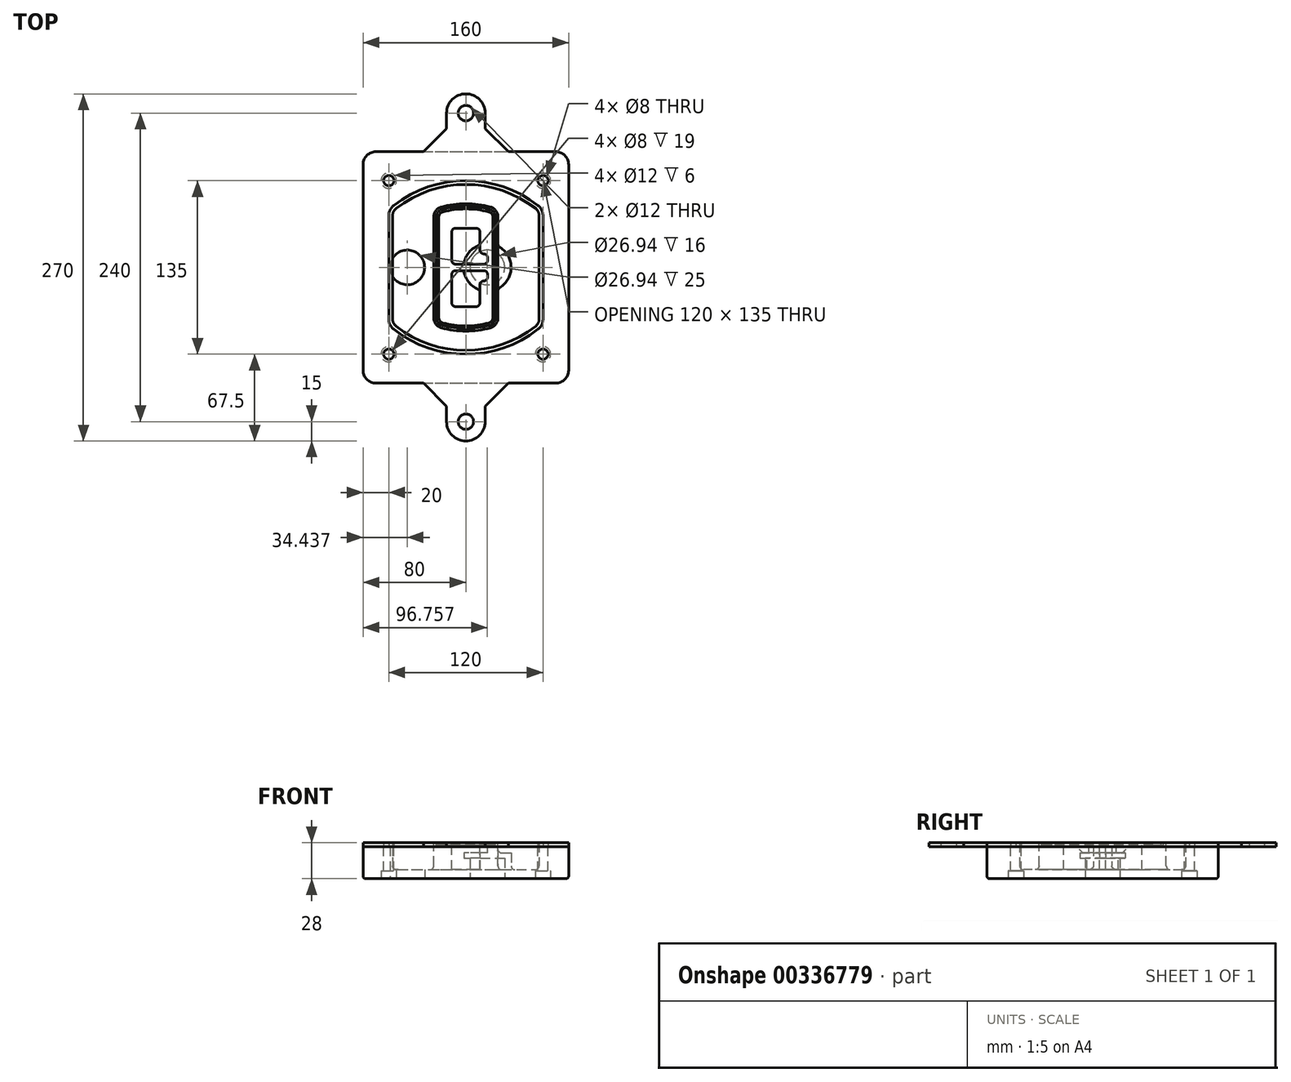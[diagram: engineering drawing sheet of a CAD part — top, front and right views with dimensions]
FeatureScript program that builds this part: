
annotation { "Feature Type Name" : "Feature", "Feature Type Description" : "" }
export const myFeature = defineFeature(function(context is Context, id is Id, definition is map)
    precondition{}
    {
        {
            var Q0;
            Q0=qCreatedBy(makeId("Top.planeOp"),FACE);
            var sketch = newSketch(context, id + "F0", { "sketchPlane" : qUnion([Q0])});
            skPoint(sketch, "E0.rect.middle", {"position": v(0, 0) * mm});
            skLineSegment(sketch, "E1.bottom", {"start": v(-70, -90) * mm, "end": v(70, -90) * mm});
            skLineSegment(sketch, "E1.top", {"start": v(-70, 90) * mm, "end": v(70, 90) * mm});
            skLineSegment(sketch, "E1.left", {"start": v(-80, -80) * mm, "end": v(-80, 80) * mm});
            skLineSegment(sketch, "E1.right", {"start": v(80, -80) * mm, "end": v(80, 80) * mm});
            skLineSegment(sketch, "E2", {"start": v(-80, 90) * mm, "end": v(80, -90) * mm, "construction": true});
            skLineSegment(sketch, "E3", {"start": v(80, 90) * mm, "end": v(-80, -90) * mm, "construction": true});
            skCircle(sketch, "E4", {"center": v(-60, 67.5) * mm, "radius": 4 * mm});
            skCircle(sketch, "E5", {"center": v(60, 67.5) * mm, "radius": 4 * mm});
            skCircle(sketch, "E6", {"center": v(60, -67.5) * mm, "radius": 4 * mm});
            skCircle(sketch, "E7", {"center": v(-60, -67.5) * mm, "radius": 4 * mm});
            skLineSegment(sketch, "E8", {"start": v(-60, 67.5) * mm, "end": v(60, 67.5) * mm, "construction": true});
            skLineSegment(sketch, "E9", {"start": v(60, 67.5) * mm, "end": v(60, -67.5) * mm, "construction": true});
            skLineSegment(sketch, "E10", {"start": v(60, -67.5) * mm, "end": v(-60, -67.5) * mm, "construction": true});
            skLineSegment(sketch, "E11", {"start": v(-60, -67.5) * mm, "end": v(-60, 67.5) * mm, "construction": true});
            skLineSegment(sketch, "E12", {"start": v(-60, 40.3) * mm, "end": v(-60, -40.3) * mm});
            skLineSegment(sketch, "E13", {"start": v(60, 40.3) * mm, "end": v(60, -40.3) * mm});
            skArc(sketch, "E14", {"start": v(56.15, 48.18) * mm, "mid": v(0, 67.5) * mm, "end": v(-56.15, 48.18) * mm});
            skArc(sketch, "E15", {"start": v(-56.15, -48.18) * mm, "mid": v(0, -67.5) * mm, "end": v(56.15, -48.18) * mm});
            skLineSegment(sketch, "E16", {"start": v(-60, 0) * mm, "end": v(60, 0) * mm, "construction": true});
            skPoint(sketch, "E17.visualSharp", {"position": v(-60, -45) * mm});
            skArc(sketch, "E17.filletArc", {"start": v(-60, -40.3) * mm, "mid": v(-58.99, -44.68) * mm, "end": v(-56.15, -48.18) * mm});
            skPoint(sketch, "E18.visualSharp", {"position": v(-60, 45) * mm});
            skArc(sketch, "E18.filletArc", {"start": v(-56.15, 48.18) * mm, "mid": v(-58.99, 44.68) * mm, "end": v(-60, 40.3) * mm});
            skPoint(sketch, "E19.visualSharp", {"position": v(60, 45) * mm});
            skArc(sketch, "E19.filletArc", {"start": v(60, 40.3) * mm, "mid": v(58.99, 44.68) * mm, "end": v(56.15, 48.18) * mm});
            skPoint(sketch, "E20.visualSharp", {"position": v(60, -45) * mm});
            skArc(sketch, "E20.filletArc", {"start": v(56.15, -48.18) * mm, "mid": v(58.99, -44.68) * mm, "end": v(60, -40.3) * mm});
            skPoint(sketch, "E21.visualSharp", {"position": v(-80, 90) * mm});
            skArc(sketch, "E21.filletArc", {"start": v(-70, 90) * mm, "mid": v(-77.07, 87.07) * mm, "end": v(-80, 80) * mm});
            skPoint(sketch, "E22.visualSharp", {"position": v(80, 90) * mm});
            skArc(sketch, "E22.filletArc", {"start": v(80, 80) * mm, "mid": v(77.07, 87.07) * mm, "end": v(70, 90) * mm});
            skPoint(sketch, "E23.visualSharp", {"position": v(80, -90) * mm});
            skArc(sketch, "E23.filletArc", {"start": v(70, -90) * mm, "mid": v(77.07, -87.07) * mm, "end": v(80, -80) * mm});
            skPoint(sketch, "E24.visualSharp", {"position": v(-80, -90) * mm});
            skArc(sketch, "E24.filletArc", {"start": v(-80, -80) * mm, "mid": v(-77.07, -87.07) * mm, "end": v(-70, -90) * mm});
            skArc(sketch, "E25.0", {"start": v(57, 40.3) * mm, "mid": v(56.3, 43.36) * mm, "end": v(54.3, 45.81) * mm});
            skLineSegment(sketch, "E25.1", {"start": v(57, 40.3) * mm, "end": v(57, -40.3) * mm});
            skArc(sketch, "E25.2", {"start": v(54.3, -45.81) * mm, "mid": v(56.3, -43.36) * mm, "end": v(57, -40.3) * mm});
            skArc(sketch, "E25.3", {"start": v(-54.3, -45.81) * mm, "mid": v(0, -64.5) * mm, "end": v(54.3, -45.81) * mm});
            skArc(sketch, "E25.4", {"start": v(-57, -40.3) * mm, "mid": v(-56.3, -43.36) * mm, "end": v(-54.3, -45.81) * mm});
            skArc(sketch, "E25.5", {"start": v(54.3, 45.81) * mm, "mid": v(0, 64.5) * mm, "end": v(-54.3, 45.81) * mm});
            skLineSegment(sketch, "E25.6", {"start": v(-57, 40.3) * mm, "end": v(-57, -40.3) * mm});
            skArc(sketch, "E25.7", {"start": v(-54.3, 45.81) * mm, "mid": v(-56.3, 43.36) * mm, "end": v(-57, 40.3) * mm});
            skArc(sketch, "E26.0", {"start": v(-58.62, 51.33) * mm, "mid": v(-62.58, 46.43) * mm, "end": v(-64, 40.3) * mm});
            skArc(sketch, "E26.1", {"start": v(58.62, 51.33) * mm, "mid": v(0, 71.5) * mm, "end": v(-58.62, 51.33) * mm});
            skArc(sketch, "E26.2", {"start": v(64, 40.3) * mm, "mid": v(62.58, 46.43) * mm, "end": v(58.62, 51.33) * mm});
            skLineSegment(sketch, "E26.3", {"start": v(64, 40.3) * mm, "end": v(64, -40.3) * mm});
            skArc(sketch, "E26.4", {"start": v(58.62, -51.33) * mm, "mid": v(62.58, -46.43) * mm, "end": v(64, -40.3) * mm});
            skLineSegment(sketch, "E26.5", {"start": v(-64, 40.3) * mm, "end": v(-64, -40.3) * mm});
            skArc(sketch, "E26.6", {"start": v(-58.62, -51.33) * mm, "mid": v(0, -71.5) * mm, "end": v(58.62, -51.33) * mm});
            skArc(sketch, "E26.7", {"start": v(-64, -40.3) * mm, "mid": v(-62.58, -46.43) * mm, "end": v(-58.62, -51.33) * mm});
            skSolve(sketch);
        }
        {
            var Q0;
            Q0=makeQuery(id+"F0.imprint","IMPRINT",FACE,{"disambiguationData":[TD([[makeQuery(id+"F0.imprint","IMPRINT",EDGE,{"derivedFrom":sQuery(id+"F0.wireOp",EDGE,"E1.bottom")}),1.0]])]});
            var Q1;
            Q1=makeQuery(id+"F0.imprint","IMPRINT",FACE,{"disambiguationData":[TD([[makeQuery(id+"F0.imprint","IMPRINT",EDGE,{"derivedFrom":sQuery(id+"F0.wireOp",EDGE,"E12")}),1.0]])]});
            var Q2;
            Q2=makeQuery(id+"F0.imprint","IMPRINT",FACE,{"disambiguationData":[TD([[makeQuery(id+"F0.imprint","IMPRINT",EDGE,{"derivedFrom":sQuery(id+"F0.wireOp",EDGE,"E25.0")}),1.0]])]});
            var Q3;
            Q3=makeQuery(id+"F0.imprint","IMPRINT",FACE,{"disambiguationData":[TD([[makeQuery(id+"F0.imprint","IMPRINT",EDGE,{"derivedFrom":sQuery(id+"F0.wireOp",EDGE,"E12")}),-1.0]])]});
            extrude(context, id + "F1", {"entities" : qUnion([Q0, Q1, Q2, Q3]), "oppositeDirection" : true, "depth" : 25 * mm});
        }
        {
            var Q0;
            Q0=makeQuery(id+"F0.imprint","IMPRINT",FACE,{"disambiguationData":[TD([[makeQuery(id+"F0.imprint","IMPRINT",EDGE,{"derivedFrom":sQuery(id+"F0.wireOp",EDGE,"E12")}),1.0]])]});
            extrude(context, id + "F2", {"entities" : qUnion([Q0]), "operationType" : NewBodyOperationType.ADD, "depth" : 3 * mm});
        }
        {
            var Q0;
            Q0=makeQuery(id+"F0.imprint","IMPRINT",FACE,{"disambiguationData":[TD([[makeQuery(id+"F0.imprint","IMPRINT",EDGE,{"derivedFrom":sQuery(id+"F0.wireOp",EDGE,"E25.0")}),1.0]])]});
            extrude(context, id + "F3", {"entities" : qUnion([Q0]), "operationType" : NewBodyOperationType.REMOVE, "oppositeDirection" : true, "depth" : 18 * mm});
        }
        {
            var Q0;
            Q0=makeQuery(id+"F2.opExtrude","CAP_FACE",FACE,{"disambiguationData":[OSD([sQuery(id+"F0.wireOp",EDGE,"E12"),sQuery(id+"F0.wireOp",EDGE,"E13"),sQuery(id+"F0.wireOp",EDGE,"E14"),sQuery(id+"F0.wireOp",EDGE,"E15"),sQuery(id+"F0.wireOp",EDGE,"E17.filletArc"),sQuery(id+"F0.wireOp",EDGE,"E18.filletArc"),sQuery(id+"F0.wireOp",EDGE,"E19.filletArc"),sQuery(id+"F0.wireOp",EDGE,"E20.filletArc"),sQuery(id+"F0.wireOp",EDGE,"E25.0"),sQuery(id+"F0.wireOp",EDGE,"E25.1"),sQuery(id+"F0.wireOp",EDGE,"E25.2"),sQuery(id+"F0.wireOp",EDGE,"E25.3"),sQuery(id+"F0.wireOp",EDGE,"E25.4"),sQuery(id+"F0.wireOp",EDGE,"E25.5"),sQuery(id+"F0.wireOp",EDGE,"E25.6"),sQuery(id+"F0.wireOp",EDGE,"E25.7")])],"isStart":false});
            var sketch = newSketch(context, id + "F4", { "sketchPlane" : qUnion([Q0])});
            skArc(sketch, "E27.0", {"start": v(-19.08, -46.97) * mm, "mid": v(0, -49.5) * mm, "end": v(19.08, -46.97) * mm});
            skArc(sketch, "E28.0", {"start": v(19.08, 46.97) * mm, "mid": v(0, 49.5) * mm, "end": v(-19.08, 46.97) * mm});
            skLineSegment(sketch, "E29", {"start": v(-25, 39.25) * mm, "end": v(-25, -39.25) * mm});
            skLineSegment(sketch, "E30", {"start": v(25, 39.25) * mm, "end": v(25, -39.25) * mm});
            skLineSegment(sketch, "E31", {"start": v(-25, 45.1) * mm, "end": v(25, 45.1) * mm, "construction": true});
            skLineSegment(sketch, "E32", {"start": v(-25, -45.1) * mm, "end": v(25, -45.1) * mm, "construction": true});
            skPoint(sketch, "E33.visualSharp", {"position": v(-25, 45.1) * mm});
            skArc(sketch, "E33.filletArc", {"start": v(-19.08, 46.97) * mm, "mid": v(-23.35, 44.11) * mm, "end": v(-25, 39.25) * mm});
            skPoint(sketch, "E34.visualSharp", {"position": v(25, 45.1) * mm});
            skArc(sketch, "E34.filletArc", {"start": v(25, 39.25) * mm, "mid": v(23.35, 44.11) * mm, "end": v(19.08, 46.97) * mm});
            skPoint(sketch, "E35.visualSharp", {"position": v(25, -45.1) * mm});
            skArc(sketch, "E35.filletArc", {"start": v(19.08, -46.97) * mm, "mid": v(23.35, -44.11) * mm, "end": v(25, -39.25) * mm});
            skPoint(sketch, "E36.visualSharp", {"position": v(-25, -45.1) * mm});
            skArc(sketch, "E36.filletArc", {"start": v(-25, -39.25) * mm, "mid": v(-23.35, -44.11) * mm, "end": v(-19.08, -46.97) * mm});
            skArc(sketch, "E37.0", {"start": v(54.3, 45.81) * mm, "mid": v(0, 64.5) * mm, "end": v(-54.3, 45.81) * mm});
            skArc(sketch, "E37.1", {"start": v(-54.3, 45.81) * mm, "mid": v(-56.3, 43.36) * mm, "end": v(-57, 40.3) * mm});
            skLineSegment(sketch, "E37.2", {"start": v(-57, 40.3) * mm, "end": v(-57, -40.3) * mm});
            skArc(sketch, "E37.3", {"start": v(-57, -40.3) * mm, "mid": v(-56.3, -43.36) * mm, "end": v(-54.3, -45.81) * mm});
            skArc(sketch, "E37.4", {"start": v(-54.3, -45.81) * mm, "mid": v(0, -64.5) * mm, "end": v(54.3, -45.81) * mm});
            skArc(sketch, "E37.5", {"start": v(54.3, -45.81) * mm, "mid": v(56.3, -43.36) * mm, "end": v(57, -40.3) * mm});
            skLineSegment(sketch, "E37.6", {"start": v(57, 40.3) * mm, "end": v(57, -40.3) * mm});
            skArc(sketch, "E37.7", {"start": v(57, 40.3) * mm, "mid": v(56.3, 43.36) * mm, "end": v(54.3, 45.81) * mm});
            skLineSegment(sketch, "E38.0", {"start": v(23, 39.25) * mm, "end": v(23, -39.25) * mm});
            skArc(sketch, "E38.1", {"start": v(18.56, -45.04) * mm, "mid": v(21.76, -42.9) * mm, "end": v(23, -39.25) * mm});
            skArc(sketch, "E38.2", {"start": v(-18.56, -45.04) * mm, "mid": v(0, -47.5) * mm, "end": v(18.56, -45.04) * mm});
            skArc(sketch, "E38.3", {"start": v(-23, -39.25) * mm, "mid": v(-21.76, -42.9) * mm, "end": v(-18.56, -45.04) * mm});
            skLineSegment(sketch, "E38.4", {"start": v(-23, 39.25) * mm, "end": v(-23, -39.25) * mm});
            skArc(sketch, "E38.5", {"start": v(23, 39.25) * mm, "mid": v(21.76, 42.9) * mm, "end": v(18.56, 45.04) * mm});
            skArc(sketch, "E38.6", {"start": v(-18.56, 45.04) * mm, "mid": v(-21.76, 42.9) * mm, "end": v(-23, 39.25) * mm});
            skArc(sketch, "E38.7", {"start": v(18.56, 45.04) * mm, "mid": v(0, 47.5) * mm, "end": v(-18.56, 45.04) * mm});
            skArc(sketch, "E39.0", {"start": v(21, 39.25) * mm, "mid": v(20.18, 41.68) * mm, "end": v(18.04, 43.1) * mm});
            skLineSegment(sketch, "E39.1", {"start": v(21, 39.25) * mm, "end": v(21, -39.25) * mm});
            skArc(sketch, "E39.2", {"start": v(18.04, -43.1) * mm, "mid": v(20.18, -41.68) * mm, "end": v(21, -39.25) * mm});
            skArc(sketch, "E39.3", {"start": v(-18.04, -43.1) * mm, "mid": v(0, -45.5) * mm, "end": v(18.04, -43.1) * mm});
            skArc(sketch, "E39.4", {"start": v(-21, -39.25) * mm, "mid": v(-20.18, -41.68) * mm, "end": v(-18.04, -43.1) * mm});
            skArc(sketch, "E39.5", {"start": v(18.04, 43.1) * mm, "mid": v(0, 45.5) * mm, "end": v(-18.04, 43.1) * mm});
            skLineSegment(sketch, "E39.6", {"start": v(-21, 39.25) * mm, "end": v(-21, -39.25) * mm});
            skArc(sketch, "E39.7", {"start": v(-18.04, 43.1) * mm, "mid": v(-20.18, 41.68) * mm, "end": v(-21, 39.25) * mm});
            skLineSegment(sketch, "E40", {"start": v(-25, 0) * mm, "end": v(25, 0) * mm, "construction": true});
            skLineSegment(sketch, "E41", {"start": v(-11, 5.5) * mm, "end": v(-11, 27.5) * mm});
            skLineSegment(sketch, "E42", {"start": v(-8, 30.5) * mm, "end": v(8, 30.5) * mm});
            skLineSegment(sketch, "E43", {"start": v(11, 27.5) * mm, "end": v(11, 13.5) * mm});
            skLineSegment(sketch, "E44", {"start": v(14, 10.5) * mm, "end": v(14, 10.5) * mm});
            skLineSegment(sketch, "E45", {"start": v(17, 7.5) * mm, "end": v(17, 5.5) * mm});
            skLineSegment(sketch, "E46", {"start": v(14, 2.5) * mm, "end": v(-8, 2.5) * mm});
            skPoint(sketch, "E47.visualSharp", {"position": v(-11, 30.5) * mm});
            skArc(sketch, "E47.filletArc", {"start": v(-8, 30.5) * mm, "mid": v(-10.12, 29.62) * mm, "end": v(-11, 27.5) * mm});
            skPoint(sketch, "E48.visualSharp", {"position": v(11, 30.5) * mm});
            skArc(sketch, "E48.filletArc", {"start": v(11, 27.5) * mm, "mid": v(10.12, 29.62) * mm, "end": v(8, 30.5) * mm});
            skPoint(sketch, "E49.visualSharp", {"position": v(11, 10.5) * mm});
            skArc(sketch, "E49.filletArc", {"start": v(11, 13.5) * mm, "mid": v(11.88, 11.38) * mm, "end": v(14, 10.5) * mm});
            skPoint(sketch, "E50.visualSharp", {"position": v(17, 10.5) * mm});
            skArc(sketch, "E50.filletArc", {"start": v(17, 7.5) * mm, "mid": v(16.12, 9.62) * mm, "end": v(14, 10.5) * mm});
            skPoint(sketch, "E51.visualSharp", {"position": v(17, 2.5) * mm});
            skArc(sketch, "E51.filletArc", {"start": v(14, 2.5) * mm, "mid": v(16.12, 3.38) * mm, "end": v(17, 5.5) * mm});
            skPoint(sketch, "E52.visualSharp", {"position": v(-11, 2.5) * mm});
            skArc(sketch, "E52.filletArc", {"start": v(-11, 5.5) * mm, "mid": v(-10.12, 3.38) * mm, "end": v(-8, 2.5) * mm});
            skLineSegment(sketch, "E53.0.MirrorCS", {"start": v(14, -2.5) * mm, "end": v(-8, -2.5) * mm});
            skArc(sketch, "E54.0.MirrorCS", {"start": v(-11, -5.5) * mm, "mid": v(-10.12, -3.38) * mm, "end": v(-8, -2.5) * mm});
            skLineSegment(sketch, "E55.0.MirrorCS", {"start": v(-11, -5.5) * mm, "end": v(-11, -27.5) * mm});
            skArc(sketch, "E56.0.MirrorCS", {"start": v(-8, -30.5) * mm, "mid": v(-10.12, -29.62) * mm, "end": v(-11, -27.5) * mm});
            skLineSegment(sketch, "E57.0.MirrorCS", {"start": v(-8, -30.5) * mm, "end": v(8, -30.5) * mm});
            skArc(sketch, "E58.0.MirrorCS", {"start": v(11, -27.5) * mm, "mid": v(10.12, -29.62) * mm, "end": v(8, -30.5) * mm});
            skLineSegment(sketch, "E59.0.MirrorCS", {"start": v(11, -27.5) * mm, "end": v(11, -13.5) * mm});
            skArc(sketch, "E60.0.MirrorCS", {"start": v(11, -13.5) * mm, "mid": v(11.88, -11.38) * mm, "end": v(14, -10.5) * mm});
            skArc(sketch, "E61.0.MirrorCS", {"start": v(17, -7.5) * mm, "mid": v(16.12, -9.62) * mm, "end": v(14, -10.5) * mm});
            skLineSegment(sketch, "E62.0.MirrorCS", {"start": v(17, -7.5) * mm, "end": v(17, -5.5) * mm});
            skArc(sketch, "E63.0.MirrorCS", {"start": v(14, -2.5) * mm, "mid": v(16.12, -3.38) * mm, "end": v(17, -5.5) * mm});
            skSolve(sketch);
        }
        {
            var Q0;
            Q0=makeQuery(id+"F4.imprint","IMPRINT",FACE,{"disambiguationData":[TD([[makeQuery(id+"F4.imprint","IMPRINT",EDGE,{"derivedFrom":sQuery(id+"F4.wireOp",EDGE,"E27.0")}),1.0]])]});
            var Q1;
            Q1=makeQuery(id+"F4.imprint","IMPRINT",FACE,{"disambiguationData":[TD([[makeQuery(id+"F4.imprint","IMPRINT",EDGE,{"derivedFrom":sQuery(id+"F4.wireOp",EDGE,"E38.0")}),-1.0]])]});
            var Q2;
            Q2=makeQuery(id+"F4.imprint","IMPRINT",FACE,{"disambiguationData":[TD([[makeQuery(id+"F4.imprint","IMPRINT",EDGE,{"derivedFrom":sQuery(id+"F4.wireOp",EDGE,"E39.0")}),1.0]])]});
            extrude(context, id + "F5", {"entities" : qUnion([Q0, Q1, Q2]), "operationType" : NewBodyOperationType.ADD, "endBound" : BoundingType.UP_TO_NEXT, "oppositeDirection" : true, "depth" : 25 * mm});
        }
        {
            var Q0;
            Q0=makeQuery(id+"F4.imprint","IMPRINT",FACE,{"disambiguationData":[TD([[makeQuery(id+"F4.imprint","IMPRINT",EDGE,{"derivedFrom":sQuery(id+"F4.wireOp",EDGE,"E38.0")}),-1.0]])]});
            extrude(context, id + "F6", {"entities" : qUnion([Q0]), "operationType" : NewBodyOperationType.REMOVE, "oppositeDirection" : true, "depth" : 2 * mm});
        }
        {
            var Q0;
            Q0=makeQuery(id+"F1.opExtrude","CAP_FACE",FACE,{"disambiguationData":[OSD([sQuery(id+"F0.wireOp",EDGE,"E1.bottom"),sQuery(id+"F0.wireOp",EDGE,"E1.top"),sQuery(id+"F0.wireOp",EDGE,"E1.left"),sQuery(id+"F0.wireOp",EDGE,"E1.right"),sQuery(id+"F0.wireOp",EDGE,"E4"),sQuery(id+"F0.wireOp",EDGE,"E5"),sQuery(id+"F0.wireOp",EDGE,"E6"),sQuery(id+"F0.wireOp",EDGE,"E7"),sQuery(id+"F0.wireOp",EDGE,"E21.filletArc"),sQuery(id+"F0.wireOp",EDGE,"E22.filletArc"),sQuery(id+"F0.wireOp",EDGE,"E23.filletArc"),sQuery(id+"F0.wireOp",EDGE,"E24.filletArc")])],"isStart":false});
            var sketch = newSketch(context, id + "F7", { "sketchPlane" : qUnion([Q0])});
            skCircle(sketch, "E64", {"center": v(16.76, 0) * mm, "radius": 13.47 * mm});
            skCircle(sketch, "E65", {"center": v(-45.56, 0) * mm, "radius": 13.47 * mm});
            skLineSegment(sketch, "E66", {"start": v(80, 0) * mm, "end": v(-80, 0) * mm});
            skCircle(sketch, "E67", {"center": v(16.76, 0) * mm, "radius": 18.47 * mm});
            skCircle(sketch, "E68", {"center": v(60, -67.5) * mm, "radius": 6 * mm});
            skCircle(sketch, "E69", {"center": v(-60, -67.5) * mm, "radius": 6 * mm});
            skCircle(sketch, "E70", {"center": v(-60, 67.5) * mm, "radius": 6 * mm});
            skCircle(sketch, "E71", {"center": v(60, 67.5) * mm, "radius": 6 * mm});
            skSolve(sketch);
        }
        {
            var Q0;
            {var subQ1=sQuery(id+"F7.wireOp",EDGE,"E66");var subQ4=sQuery(id+"F7.wireOp",EDGE,"E64");var subQ6=makeQuery(id+"F7.imprint","INTERSECT",VERTEX,{"disambiguationData":[OD(0.0)],"derivedFrom":[subQ4,subQ1]});Q0=makeQuery(id+"F7.imprint","IMPRINT",FACE,{"disambiguationData":[TD([[makeQuery(id+"F7.imprint","IMPRINT",EDGE,{"disambiguationData":[TD([[subQ6,-1.0]])],"derivedFrom":subQ4}),-1.0]])]});}
            var Q1;
            {var subQ0=sQuery(id+"F7.wireOp",EDGE,"E66");var subQ1=sQuery(id+"F7.wireOp",EDGE,"E64");var subQ3=makeQuery(id+"F7.imprint","INTERSECT",VERTEX,{"disambiguationData":[OD(0.0)],"derivedFrom":[subQ1,subQ0]});Q1=makeQuery(id+"F7.imprint","IMPRINT",FACE,{"disambiguationData":[TD([[makeQuery(id+"F7.imprint","IMPRINT",EDGE,{"disambiguationData":[TD([[subQ3,-1.0]])],"derivedFrom":subQ1}),1.0]])]});}
            var Q2;
            {var subQ0=sQuery(id+"F7.wireOp",EDGE,"E66");var subQ1=sQuery(id+"F7.wireOp",EDGE,"E64");var subQ3=makeQuery(id+"F7.imprint","INTERSECT",VERTEX,{"disambiguationData":[OD(0.0)],"derivedFrom":[subQ1,subQ0]});Q2=makeQuery(id+"F7.imprint","IMPRINT",FACE,{"disambiguationData":[TD([[makeQuery(id+"F7.imprint","IMPRINT",EDGE,{"disambiguationData":[TD([[subQ3,1.0]])],"derivedFrom":subQ1}),1.0]])]});}
            var Q3;
            {var subQ1=sQuery(id+"F7.wireOp",EDGE,"E66");var subQ4=sQuery(id+"F7.wireOp",EDGE,"E64");var subQ6=makeQuery(id+"F7.imprint","INTERSECT",VERTEX,{"disambiguationData":[OD(0.0)],"derivedFrom":[subQ4,subQ1]});Q3=makeQuery(id+"F7.imprint","IMPRINT",FACE,{"disambiguationData":[TD([[makeQuery(id+"F7.imprint","IMPRINT",EDGE,{"disambiguationData":[TD([[subQ6,1.0]])],"derivedFrom":subQ4}),-1.0]])]});}
            extrude(context, id + "F8", {"entities" : qUnion([Q0, Q1, Q2, Q3]), "operationType" : NewBodyOperationType.ADD, "oppositeDirection" : true, "depth" : 20 * mm});
        }
        {
            var Q0;
            {var subQ0=sQuery(id+"F7.wireOp",EDGE,"E66");var subQ1=sQuery(id+"F7.wireOp",EDGE,"E64");var subQ3=makeQuery(id+"F7.imprint","INTERSECT",VERTEX,{"disambiguationData":[OD(0.0)],"derivedFrom":[subQ1,subQ0]});Q0=makeQuery(id+"F7.imprint","IMPRINT",FACE,{"disambiguationData":[TD([[makeQuery(id+"F7.imprint","IMPRINT",EDGE,{"disambiguationData":[TD([[subQ3,-1.0]])],"derivedFrom":subQ1}),1.0]])]});}
            var Q1;
            {var subQ0=sQuery(id+"F7.wireOp",EDGE,"E66");var subQ1=sQuery(id+"F7.wireOp",EDGE,"E64");var subQ3=makeQuery(id+"F7.imprint","INTERSECT",VERTEX,{"disambiguationData":[OD(0.0)],"derivedFrom":[subQ1,subQ0]});Q1=makeQuery(id+"F7.imprint","IMPRINT",FACE,{"disambiguationData":[TD([[makeQuery(id+"F7.imprint","IMPRINT",EDGE,{"disambiguationData":[TD([[subQ3,1.0]])],"derivedFrom":subQ1}),1.0]])]});}
            extrude(context, id + "F9", {"entities" : qUnion([Q0, Q1]), "operationType" : NewBodyOperationType.REMOVE, "oppositeDirection" : true, "depth" : 16 * mm});
        }
        {
            var Q0;
            {var subQ0=sQuery(id+"F7.wireOp",EDGE,"E66");var subQ1=sQuery(id+"F7.wireOp",EDGE,"E65");var subQ3=makeQuery(id+"F7.imprint","INTERSECT",VERTEX,{"disambiguationData":[OD(0.0)],"derivedFrom":[subQ1,subQ0]});Q0=makeQuery(id+"F7.imprint","IMPRINT",FACE,{"disambiguationData":[TD([[makeQuery(id+"F7.imprint","IMPRINT",EDGE,{"disambiguationData":[TD([[subQ3,-1.0]])],"derivedFrom":subQ1}),1.0]])]});}
            var Q1;
            {var subQ0=sQuery(id+"F7.wireOp",EDGE,"E66");var subQ1=sQuery(id+"F7.wireOp",EDGE,"E65");var subQ3=makeQuery(id+"F7.imprint","INTERSECT",VERTEX,{"disambiguationData":[OD(0.0)],"derivedFrom":[subQ1,subQ0]});Q1=makeQuery(id+"F7.imprint","IMPRINT",FACE,{"disambiguationData":[TD([[makeQuery(id+"F7.imprint","IMPRINT",EDGE,{"disambiguationData":[TD([[subQ3,1.0]])],"derivedFrom":subQ1}),1.0]])]});}
            extrude(context, id + "F10", {"entities" : qUnion([Q0, Q1]), "operationType" : NewBodyOperationType.REMOVE, "oppositeDirection" : true, "depth" : 25 * mm});
        }
        {
            var Q0;
            Q0=makeQuery(id+"F7.imprint","IMPRINT",FACE,{"disambiguationData":[TD([[makeQuery(id+"F7.imprint","IMPRINT",EDGE,{"derivedFrom":sQuery(id+"F7.wireOp",EDGE,"E68")}),1.0]])]});
            var Q1;
            Q1=makeQuery(id+"F7.imprint","IMPRINT",FACE,{"disambiguationData":[TD([[makeQuery(id+"F7.imprint","IMPRINT",EDGE,{"derivedFrom":makeQuery(id+"F1.opExtrude","CAP_EDGE",EDGE,{"disambiguationData":[OSD([sQuery(id+"F0.wireOp",EDGE,"E5")])],"isStart":false})}),-1.0]])]});
            var Q2;
            Q2=makeQuery(id+"F7.imprint","IMPRINT",FACE,{"disambiguationData":[TD([[makeQuery(id+"F7.imprint","IMPRINT",EDGE,{"derivedFrom":sQuery(id+"F7.wireOp",EDGE,"E69")}),1.0]])]});
            var Q3;
            Q3=makeQuery(id+"F7.imprint","IMPRINT",FACE,{"disambiguationData":[TD([[makeQuery(id+"F7.imprint","IMPRINT",EDGE,{"derivedFrom":makeQuery(id+"F1.opExtrude","CAP_EDGE",EDGE,{"disambiguationData":[OSD([sQuery(id+"F0.wireOp",EDGE,"E4")])],"isStart":false})}),-1.0]])]});
            var Q4;
            Q4=makeQuery(id+"F7.imprint","IMPRINT",FACE,{"disambiguationData":[TD([[makeQuery(id+"F7.imprint","IMPRINT",EDGE,{"derivedFrom":sQuery(id+"F7.wireOp",EDGE,"E70")}),1.0]])]});
            var Q5;
            Q5=makeQuery(id+"F7.imprint","IMPRINT",FACE,{"disambiguationData":[TD([[makeQuery(id+"F7.imprint","IMPRINT",EDGE,{"derivedFrom":makeQuery(id+"F1.opExtrude","CAP_EDGE",EDGE,{"disambiguationData":[OSD([sQuery(id+"F0.wireOp",EDGE,"E7")])],"isStart":false})}),-1.0]])]});
            var Q6;
            Q6=makeQuery(id+"F7.imprint","IMPRINT",FACE,{"disambiguationData":[TD([[makeQuery(id+"F7.imprint","IMPRINT",EDGE,{"derivedFrom":sQuery(id+"F7.wireOp",EDGE,"E71")}),1.0]])]});
            var Q7;
            Q7=makeQuery(id+"F7.imprint","IMPRINT",FACE,{"disambiguationData":[TD([[makeQuery(id+"F7.imprint","IMPRINT",EDGE,{"derivedFrom":makeQuery(id+"F1.opExtrude","CAP_EDGE",EDGE,{"disambiguationData":[OSD([sQuery(id+"F0.wireOp",EDGE,"E6")])],"isStart":false})}),-1.0]])]});
            extrude(context, id + "F11", {"entities" : qUnion([Q0, Q1, Q2, Q3, Q4, Q5, Q6, Q7]), "operationType" : NewBodyOperationType.REMOVE, "oppositeDirection" : true, "depth" : 6 * mm});
        }
        {
            var Q0;
            Q0=makeQuery(id+"F9.boolean.opBoolean","COPY",FACE,{"derivedFrom":makeQuery(id+"F9.opExtrude","CAP_FACE",FACE,{"disambiguationData":[OSD([sQuery(id+"F7.wireOp",EDGE,"E64")])],"isStart":false})});
            var sketch = newSketch(context, id + "F12", { "sketchPlane" : qUnion([Q0])});
            skArc(sketch, "E72.0", {"start": v(11, 17.55) * mm, "mid": v(2.57, 11.82) * mm, "end": v(-1.54, 2.5) * mm});
            skArc(sketch, "E72.1", {"start": v(-1.54, -2.5) * mm, "mid": v(2.57, -11.82) * mm, "end": v(11, -17.55) * mm});
            skLineSegment(sketch, "E73", {"start": v(-1.54, -2.5) * mm, "end": v(14, -2.5) * mm});
            skLineSegment(sketch, "E74.0", {"start": v(14, 2.5) * mm, "end": v(-1.54, 2.5) * mm});
            skArc(sketch, "E74.1", {"start": v(14, 2.5) * mm, "mid": v(16.12, 3.38) * mm, "end": v(17, 5.5) * mm});
            skLineSegment(sketch, "E74.2", {"start": v(17, 7.5) * mm, "end": v(17, 5.5) * mm});
            skArc(sketch, "E74.3", {"start": v(17, 7.5) * mm, "mid": v(16.12, 9.62) * mm, "end": v(14, 10.5) * mm});
            skArc(sketch, "E74.4", {"start": v(11, 13.5) * mm, "mid": v(11.88, 11.38) * mm, "end": v(14, 10.5) * mm});
            skLineSegment(sketch, "E74.5", {"start": v(11, 17.55) * mm, "end": v(11, 13.5) * mm});
            skLineSegment(sketch, "E74.7", {"start": v(14, -2.5) * mm, "end": v(-1.54, -2.5) * mm});
            skArc(sketch, "E74.8", {"start": v(14, -2.5) * mm, "mid": v(16.12, -3.38) * mm, "end": v(17, -5.5) * mm});
            skLineSegment(sketch, "E74.9", {"start": v(17, -7.5) * mm, "end": v(17, -5.5) * mm});
            skArc(sketch, "E74.10", {"start": v(17, -7.5) * mm, "mid": v(16.12, -9.62) * mm, "end": v(14, -10.5) * mm});
            skArc(sketch, "E74.11", {"start": v(11, -13.5) * mm, "mid": v(11.88, -11.38) * mm, "end": v(14, -10.5) * mm});
            skLineSegment(sketch, "E74.12", {"start": v(11, -17.55) * mm, "end": v(11, -13.5) * mm});
            skPoint(sketch, "E75.orphan", {"position": v(11, -27.5) * mm});
            skPoint(sketch, "E76.orphan", {"position": v(-8, -2.5) * mm});
            skPoint(sketch, "E77.orphan", {"position": v(-8, 2.5) * mm});
            skPoint(sketch, "E78.orphan", {"position": v(11, 27.5) * mm});
            skSolve(sketch);
        }
        {
            var Q0;
            {var subQ7=sQuery(id+"F12.wireOp",EDGE,"E72.0");var subQ14=sQuery(id+"F12.wireOp",EDGE,"E72.1");var subQ16=sQuery(id+"F12.wireOp",EDGE,"E74.1");var subQ18=sQuery(id+"F12.wireOp",EDGE,"E74.8");Q0=qUnion([makeQuery(id+"F12.imprint","IMPRINT",FACE,{"disambiguationData":[TD([[makeQuery(id+"F12.imprint","IMPRINT",EDGE,{"derivedFrom":subQ7}),1.0]])]}),makeQuery(id+"F12.imprint","IMPRINT",FACE,{"disambiguationData":[TD([[makeQuery(id+"F12.imprint","IMPRINT",EDGE,{"derivedFrom":subQ14}),1.0]])]}),makeQuery(id+"F12.imprint","IMPRINT",FACE,{"disambiguationData":[TD([[makeQuery(id+"F12.imprint","IMPRINT",EDGE,{"derivedFrom":subQ16}),1.0]])]}),makeQuery(id+"F12.imprint","IMPRINT",FACE,{"disambiguationData":[TD([[makeQuery(id+"F12.imprint","IMPRINT",EDGE,{"derivedFrom":subQ18}),-1.0]])]})]);}
            var Q1;
            Q1=makeQuery(id+"F5.boolean.opBoolean","SPLIT",FACE,{"disambiguationData":[TD([makeQuery(id+"F5.opExtrude","SWEPT_FACE",FACE,{"disambiguationData":[OSD([sQuery(id+"F4.wireOp",EDGE,"E41")])]})])],"derivedFrom":makeQuery(id+"F3.boolean.opBoolean","COPY",FACE,{"derivedFrom":makeQuery(id+"F3.opExtrude","CAP_FACE",FACE,{"disambiguationData":[OSD([sQuery(id+"F0.wireOp",EDGE,"E25.0"),sQuery(id+"F0.wireOp",EDGE,"E25.1"),sQuery(id+"F0.wireOp",EDGE,"E25.2"),sQuery(id+"F0.wireOp",EDGE,"E25.3"),sQuery(id+"F0.wireOp",EDGE,"E25.4"),sQuery(id+"F0.wireOp",EDGE,"E25.5"),sQuery(id+"F0.wireOp",EDGE,"E25.6"),sQuery(id+"F0.wireOp",EDGE,"E25.7")])],"isStart":false})})});
            extrude(context, id + "F13", {"entities" : qUnion([Q0]), "operationType" : NewBodyOperationType.REMOVE, "endBound" : BoundingType.UP_TO_SURFACE, "endBoundEntityFace" : qUnion([Q1]), "depth" : 25 * mm});
        }
        {
            var Q0;
            Q0=makeQuery(id+"F3.boolean.opBoolean","COPY",EDGE,{"derivedFrom":makeQuery(id+"F3.opExtrude","CAP_EDGE",EDGE,{"disambiguationData":[OSD([sQuery(id+"F0.wireOp",EDGE,"E25.6")])],"isStart":false})});
            var Q1;
            Q1=makeQuery(id+"F8.boolean.opBoolean","INTERSECT",EDGE,{"derivedFrom":[makeQuery(id+"F5.opExtrude","SWEPT_FACE",FACE,{"disambiguationData":[OSD([sQuery(id+"F4.wireOp",EDGE,"E30")])]}),makeQuery(id+"F8.opExtrude","CAP_FACE",FACE,{"disambiguationData":[OSD([sQuery(id+"F7.wireOp",EDGE,"E67")])],"isStart":false})]});
            var Q2;
            Q2=makeQuery(id+"F8.boolean.opBoolean","INTERSECT",EDGE,{"disambiguationData":[OD(1.0)],"derivedFrom":[makeQuery(id+"F5.opExtrude","SWEPT_FACE",FACE,{"disambiguationData":[OSD([sQuery(id+"F4.wireOp",EDGE,"E30")])]}),makeQuery(id+"F8.opExtrude","SWEPT_FACE",FACE,{"disambiguationData":[OSD([sQuery(id+"F7.wireOp",EDGE,"E67")])]})]});
            var Q3;
            {var subQ0=sQuery(id+"F4.wireOp",EDGE,"E30");Q3=makeQuery(id+"F8.boolean.opBoolean","SPLIT",EDGE,{"disambiguationData":[TD([makeQuery(id+"F5.opExtrude","SWEPT_FACE",FACE,{"disambiguationData":[OSD([sQuery(id+"F4.wireOp",EDGE,"E35.filletArc")])]})])],"derivedFrom":makeQuery(id+"F5.opExtrude","CAP_EDGE",EDGE,{"disambiguationData":[OSD([subQ0])],"isStart":false})});}
            var Q4;
            {var subQ0=sQuery(id+"F0.wireOp",EDGE,"E25.7");var subQ1=sQuery(id+"F0.wireOp",EDGE,"E25.1");var subQ2=sQuery(id+"F0.wireOp",EDGE,"E25.6");var subQ3=sQuery(id+"F0.wireOp",EDGE,"E25.5");var subQ4=sQuery(id+"F0.wireOp",EDGE,"E25.4");var subQ5=sQuery(id+"F0.wireOp",EDGE,"E25.0");var subQ6=sQuery(id+"F0.wireOp",EDGE,"E25.2");var subQ7=sQuery(id+"F0.wireOp",EDGE,"E25.3");Q4=makeQuery(id+"F8.boolean.opBoolean","INTERSECT",EDGE,{"derivedFrom":[makeQuery(id+"F5.boolean.opBoolean","SPLIT",FACE,{"disambiguationData":[TD([makeQuery(id+"F2.opExtrude","SWEPT_FACE",FACE,{"disambiguationData":[OSD([subQ5])]})])],"derivedFrom":makeQuery(id+"F3.boolean.opBoolean","COPY",FACE,{"derivedFrom":makeQuery(id+"F3.opExtrude","CAP_FACE",FACE,{"disambiguationData":[OSD([subQ5,subQ1,subQ6,subQ7,subQ4,subQ3,subQ2,subQ0])],"isStart":false})})}),makeQuery(id+"F8.opExtrude","SWEPT_FACE",FACE,{"disambiguationData":[OSD([sQuery(id+"F7.wireOp",EDGE,"E67")])]})]});}
            var Q5;
            Q5=makeQuery(id+"F8.boolean.opBoolean","INTERSECT",EDGE,{"disambiguationData":[OD(0.0)],"derivedFrom":[makeQuery(id+"F5.opExtrude","SWEPT_FACE",FACE,{"disambiguationData":[OSD([sQuery(id+"F4.wireOp",EDGE,"E30")])]}),makeQuery(id+"F8.opExtrude","SWEPT_FACE",FACE,{"disambiguationData":[OSD([sQuery(id+"F7.wireOp",EDGE,"E67")])]})]});
            fillet(context, id + "F14", {"entities" : qUnion([Q0, Q1, Q2, Q3, Q4, Q5]), "radius" : 3 * mm, "tangentPropagation" : true, "allowEdgeOverflow" : false});
        }
        {
            var Q0;
            Q0=makeQuery(id+"F1.opExtrude","CAP_EDGE",EDGE,{"disambiguationData":[OSD([sQuery(id+"F0.wireOp",EDGE,"E1.bottom")])],"isStart":false});
            fillet(context, id + "F15", {"entities" : qUnion([Q0]), "radius" : 2 * mm, "tangentPropagation" : true, "allowEdgeOverflow" : false});
        }
        {
            var Q0;
            {var subQ0=sQuery(id+"F0.wireOp",EDGE,"E21.filletArc");var subQ1=sQuery(id+"F0.wireOp",EDGE,"E7");var subQ2=sQuery(id+"F0.wireOp",EDGE,"E6");var subQ3=sQuery(id+"F0.wireOp",EDGE,"E5");var subQ4=sQuery(id+"F0.wireOp",EDGE,"E4");var subQ5=sQuery(id+"F0.wireOp",EDGE,"E22.filletArc");var subQ6=sQuery(id+"F0.wireOp",EDGE,"E1.bottom");var subQ7=sQuery(id+"F0.wireOp",EDGE,"E1.right");var subQ8=sQuery(id+"F0.wireOp",EDGE,"E1.top");var subQ9=sQuery(id+"F0.wireOp",EDGE,"E1.left");var subQ10=sQuery(id+"F0.wireOp",EDGE,"E23.filletArc");var subQ11=sQuery(id+"F0.wireOp",EDGE,"E24.filletArc");Q0=makeQuery(id+"F2.boolean.opBoolean","SPLIT",FACE,{"disambiguationData":[TD([makeQuery(id+"F1.opExtrude","SWEPT_FACE",FACE,{"disambiguationData":[OSD([subQ6])]})])],"derivedFrom":makeQuery(id+"F1.opExtrude","CAP_FACE",FACE,{"disambiguationData":[OSD([subQ6,subQ8,subQ9,subQ7,subQ4,subQ3,subQ2,subQ1,subQ0,subQ5,subQ10,subQ11])],"isStart":true})});}
            var sketch = newSketch(context, id + "F16", { "sketchPlane" : qUnion([Q0])});
            skLineSegment(sketch, "E79", {"start": v(0, 90) * mm, "end": v(0, 120) * mm, "construction": true});
            skLineSegment(sketch, "E80", {"start": v(-33, 90) * mm, "end": v(-15, 108) * mm});
            skLineSegment(sketch, "E81", {"start": v(-15, 108) * mm, "end": v(-15, 120) * mm});
            skCircle(sketch, "E82", {"center": v(0, 120) * mm, "radius": 6 * mm});
            skArc(sketch, "E83", {"start": v(15, 120) * mm, "mid": v(0, 135) * mm, "end": v(-15, 120) * mm});
            skLineSegment(sketch, "E84.MirrorCS", {"start": v(-33, -270) * mm, "end": v(-15, -288) * mm});
            skLineSegment(sketch, "E85.MirrorCS", {"start": v(-15, -288) * mm, "end": v(-15, -300) * mm});
            skArc(sketch, "E86.MirrorCS", {"start": v(15, -300) * mm, "mid": v(0, -315) * mm, "end": v(-15, -300) * mm});
            skLineSegment(sketch, "E87.MirrorCS", {"start": v(15, -269.4) * mm, "end": v(15, -300) * mm});
            skLineSegment(sketch, "E88.MirrorCS", {"start": v(15, -269.4) * mm, "end": v(14.4, -270) * mm});
            skLineSegment(sketch, "E89", {"start": v(15, 120) * mm, "end": v(15, 108) * mm});
            skLineSegment(sketch, "E90", {"start": v(15, 108) * mm, "end": v(33, 90) * mm});
            skLineSegment(sketch, "E91", {"start": v(-80, 0) * mm, "end": v(80, 0) * mm, "construction": true});
            skLineSegment(sketch, "E92.MirrorCS", {"start": v(15, -108) * mm, "end": v(33, -90) * mm});
            skLineSegment(sketch, "E93.MirrorCS", {"start": v(15, -120) * mm, "end": v(15, -108) * mm});
            skArc(sketch, "E94.MirrorCS", {"start": v(15, -120) * mm, "mid": v(0, -135) * mm, "end": v(-15, -120) * mm});
            skLineSegment(sketch, "E95.MirrorCS", {"start": v(-15, -108) * mm, "end": v(-15, -120) * mm});
            skLineSegment(sketch, "E96.MirrorCS", {"start": v(-33, -90) * mm, "end": v(-15, -108) * mm});
            skLineSegment(sketch, "E97.MirrorCS", {"start": v(0, -90) * mm, "end": v(0, -120) * mm, "construction": true});
            skCircle(sketch, "E98.MirrorC", {"center": v(0, -120) * mm, "radius": 6 * mm});
            skSolve(sketch);
        }
        {
            var Q0;
            {var subQ0=sQuery(id+"F16.wireOp",EDGE,"E80");Q0=makeQuery(id+"F16.imprint","IMPRINT",FACE,{"disambiguationData":[TD([[makeQuery(id+"F16.imprint","IMPRINT",EDGE,{"derivedFrom":subQ0}),-1.0]])]});}
            var Q1;
            {var subQ0=sQuery(id+"F16.wireOp",EDGE,"E92.MirrorCS");Q1=makeQuery(id+"F16.imprint","IMPRINT",FACE,{"disambiguationData":[TD([[makeQuery(id+"F16.imprint","IMPRINT",EDGE,{"derivedFrom":subQ0}),1.0]])]});}
            var Q2;
            Q2=makeQuery(id+"F16.imprint","IMPRINT",FACE,{"disambiguationData":[TD([[makeQuery(id+"F16.imprint","IMPRINT",EDGE,{"derivedFrom":makeQuery(id+"F1.opExtrude","CAP_EDGE",EDGE,{"disambiguationData":[OSD([sQuery(id+"F0.wireOp",EDGE,"E1.left")])],"isStart":true})}),-1.0]])]});
            var Q3;
            Q3=makeQuery(id+"F2.opExtrude","CAP_FACE",FACE,{"disambiguationData":[OSD([sQuery(id+"F0.wireOp",EDGE,"E12"),sQuery(id+"F0.wireOp",EDGE,"E13"),sQuery(id+"F0.wireOp",EDGE,"E14"),sQuery(id+"F0.wireOp",EDGE,"E15"),sQuery(id+"F0.wireOp",EDGE,"E17.filletArc"),sQuery(id+"F0.wireOp",EDGE,"E18.filletArc"),sQuery(id+"F0.wireOp",EDGE,"E19.filletArc"),sQuery(id+"F0.wireOp",EDGE,"E20.filletArc"),sQuery(id+"F0.wireOp",EDGE,"E25.0"),sQuery(id+"F0.wireOp",EDGE,"E25.1"),sQuery(id+"F0.wireOp",EDGE,"E25.2"),sQuery(id+"F0.wireOp",EDGE,"E25.3"),sQuery(id+"F0.wireOp",EDGE,"E25.4"),sQuery(id+"F0.wireOp",EDGE,"E25.5"),sQuery(id+"F0.wireOp",EDGE,"E25.6"),sQuery(id+"F0.wireOp",EDGE,"E25.7")])],"isStart":false});
            extrude(context, id + "F17", {"entities" : qUnion([Q0, Q1, Q2]), "endBound" : BoundingType.UP_TO_SURFACE, "endBoundEntityFace" : qUnion([Q3]), "depth" : 25 * mm});
        }
    });
